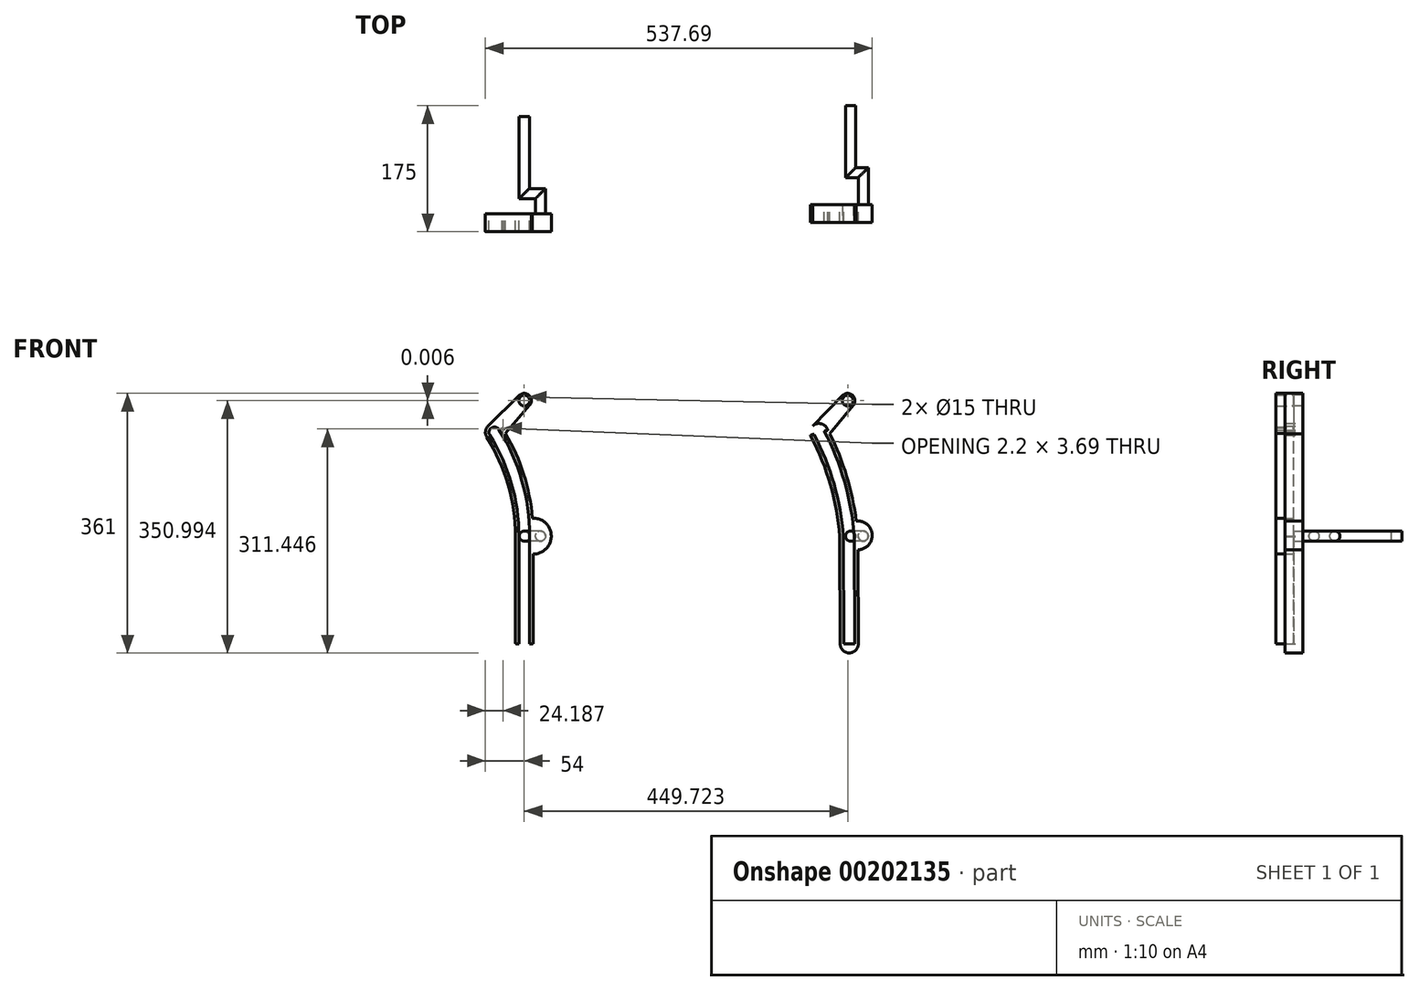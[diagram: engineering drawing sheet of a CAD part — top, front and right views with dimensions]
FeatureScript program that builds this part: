
annotation { "Feature Type Name" : "Feature", "Feature Type Description" : "" }
export const myFeature = defineFeature(function(context is Context, id is Id, definition is map)
    precondition{}
    {
        {
            var Q0;
            Q0=qCreatedBy(makeId("Front.planeOp"),FACE);
            var sketch = newSketch(context, id + "F0", { "sketchPlane" : qUnion([Q0])});
            skArc(sketch, "E0", {"start": v(451.22, 0) * mm, "mid": v(437.83, 74.2) * mm, "end": v(409.72, 144.14) * mm});
            skArc(sketch, "E1.0.startCap", {"start": v(458.7, 0.58) * mm, "mid": v(451.8, -7.48) * mm, "end": v(443.75, -0.58) * mm});
            skArc(sketch, "E1.0.endCap", {"start": v(403.08, 140.66) * mm, "mid": v(406.23, 150.78) * mm, "end": v(416.36, 147.63) * mm});
            skArc(sketch, "E1.0.left", {"start": v(443.75, -0.58) * mm, "mid": v(430.63, 72.12) * mm, "end": v(403.08, 140.66) * mm});
            skArc(sketch, "E1.0.right", {"start": v(458.7, 0.58) * mm, "mid": v(445.04, 76.27) * mm, "end": v(416.36, 147.63) * mm});
            skLineSegment(sketch, "E1.1.startCap", {"start": v(349.68, 0) * mm, "end": v(349.68, 0) * mm});
            skArc(sketch, "E2.0", {"start": v(463.69, 0.96) * mm, "mid": v(449.85, 77.65) * mm, "end": v(420.79, 149.96) * mm});
            skArc(sketch, "E3.0", {"start": v(438.72, -0.5) * mm, "mid": v(425.76, 70.95) * mm, "end": v(398.66, 138.33) * mm});
            skArc(sketch, "E4.0", {"start": v(398.66, 138.33) * mm, "mid": v(403.9, 155.2) * mm, "end": v(420.79, 149.96) * mm});
            skArc(sketch, "E5", {"start": v(463.8, -19.04) * mm, "mid": v(483.66, 2.04) * mm, "end": v(461.63, 20.85) * mm});
            skCircle(sketch, "E6", {"center": v(449.72, 188.5) * mm, "radius": 10 * mm});
            skLineSegment(sketch, "E7", {"start": v(442.58, 195.5) * mm, "end": v(400.8, 152.9) * mm});
            skLineSegment(sketch, "E8", {"start": v(457.42, 182.11) * mm, "end": v(419.35, 136.17) * mm});
            skLineSegment(sketch, "E9", {"start": v(451.22, 0) * mm, "end": v(451.8, -150) * mm});
            skPoint(sketch, "E9.endSnap0", {"position": v(451.8, -7.48) * mm});
            skArc(sketch, "E10.0.startCap", {"start": v(443.72, -0.03) * mm, "mid": v(451.2, 7.5) * mm, "end": v(458.72, 0.03) * mm});
            skArc(sketch, "E10.0.endCap", {"start": v(459.3, -149.97) * mm, "mid": v(451.83, -157.5) * mm, "end": v(444.3, -150.03) * mm});
            skLineSegment(sketch, "E10.0.left", {"start": v(458.72, 0.03) * mm, "end": v(459.3, -149.97) * mm});
            skLineSegment(sketch, "E10.0.right", {"start": v(443.72, -0.03) * mm, "end": v(444.3, -150.03) * mm});
            skLineSegment(sketch, "E11.0", {"start": v(463.72, 0.36) * mm, "end": v(464.3, -149.94) * mm});
            skLineSegment(sketch, "E12.0", {"start": v(438.72, -0.5) * mm, "end": v(439.3, -150.05) * mm});
            skArc(sketch, "E13.0", {"start": v(464.3, -149.94) * mm, "mid": v(451.85, -162.5) * mm, "end": v(439.3, -150.05) * mm});
            skLineSegment(sketch, "E14", {"start": v(438.72, -0.5) * mm, "end": v(463.69, 0.96) * mm});
            skCircle(sketch, "E15", {"center": v(451.22, 0) * mm, "radius": 188.5 * mm});
            skCircle(sketch, "E16", {"center": v(451.22, 0) * mm, "radius": 150 * mm});
            skSolve(sketch);
        }
        {
            var Q0;
            {var subQ0=sQuery(id+"F0.wireOp",EDGE,"E6");var subQ1=makeQuery(id+"F0.imprint","INTERSECT",VERTEX,{"derivedFrom":[subQ0,sQuery(id+"F0.wireOp",EDGE,"E7")]});Q0=makeQuery(id+"F0.imprint","IMPRINT",FACE,{"disambiguationData":[TD([[makeQuery(id+"F0.imprint","IMPRINT",EDGE,{"disambiguationData":[TD([[subQ1,-1.0]])],"derivedFrom":subQ0}),1.0]])]});}
            var Q1;
            {var subQ3=sQuery(id+"F0.wireOp",EDGE,"E5");Q1=makeQuery(id+"F0.imprint","IMPRINT",FACE,{"disambiguationData":[TD([[makeQuery(id+"F0.imprint","IMPRINT",EDGE,{"derivedFrom":subQ3}),1.0]])]});}
            var Q2;
            {var subQ5=sQuery(id+"F0.wireOp",EDGE,"E3.0");Q2=makeQuery(id+"F0.imprint","IMPRINT",FACE,{"disambiguationData":[TD([[makeQuery(id+"F0.imprint","IMPRINT",EDGE,{"derivedFrom":subQ5}),-1.0]])]});}
            var Q3;
            {var subQ0=sQuery(id+"F0.wireOp",EDGE,"E7");Q3=makeQuery(id+"F0.imprint","IMPRINT",FACE,{"disambiguationData":[TD([[makeQuery(id+"F0.imprint","IMPRINT",EDGE,{"derivedFrom":subQ0}),1.0]])]});}
            var Q4;
            {var subQ0=sQuery(id+"F0.wireOp",EDGE,"E10.0.right");Q4=makeQuery(id+"F0.imprint","IMPRINT",FACE,{"disambiguationData":[TD([[makeQuery(id+"F0.imprint","IMPRINT",EDGE,{"derivedFrom":subQ0}),-1.0]])]});}
            var Q5;
            {var subQ1=sQuery(id+"F0.wireOp",EDGE,"E2.0");var subQ5=makeQuery(id+"F0.imprint","INTERSECT",VERTEX,{"derivedFrom":[subQ1,sQuery(id+"F0.wireOp",EDGE,"E5")]});Q5=makeQuery(id+"F0.imprint","IMPRINT",FACE,{"disambiguationData":[TD([[makeQuery(id+"F0.imprint","IMPRINT",EDGE,{"disambiguationData":[TD([[subQ5,-1.0]])],"derivedFrom":subQ1}),1.0]])]});}
            var Q6;
            {var subQ0=sQuery(id+"F0.wireOp",EDGE,"E8");var subQ1=sQuery(id+"F0.wireOp",EDGE,"E1.0.right");var subQ2=makeQuery(id+"F0.imprint","INTERSECT",VERTEX,{"derivedFrom":[subQ1,subQ0]});Q6=makeQuery(id+"F0.imprint","IMPRINT",FACE,{"disambiguationData":[TD([[makeQuery(id+"F0.imprint","IMPRINT",EDGE,{"disambiguationData":[TD([[subQ2,-1.0]])],"derivedFrom":subQ1}),-1.0]])]});}
            var Q7;
            {var subQ6=sQuery(id+"F0.wireOp",EDGE,"E10.0.endCap");Q7=makeQuery(id+"F0.imprint","IMPRINT",FACE,{"disambiguationData":[TD([[makeQuery(id+"F0.imprint","IMPRINT",EDGE,{"derivedFrom":subQ6}),1.0]])]});}
            var Q8;
            {var subQ0=sQuery(id+"F0.wireOp",EDGE,"y67nMwY5-X2Z8-XgEG-YsyU-s40BRp6oOK45");var subQ1=sQuery(id+"F0.wireOp",EDGE,"zbyQ8gM6-2aZd-Salr-UTL1-q6hNuw3ZyB9F");var subQ2=makeQuery(id+"F0.imprint","INTERSECT",VERTEX,{"disambiguationData":[OD(0.0)],"derivedFrom":[subQ1,subQ0]});Q8=makeQuery(id+"F0.imprint","IMPRINT",FACE,{"disambiguationData":[TD([[makeQuery(id+"F0.imprint","IMPRINT",EDGE,{"disambiguationData":[TD([[subQ2,-1.0]])],"derivedFrom":subQ1}),-1.0]])]});}
            var Q9;
            {var subQ0=sQuery(id+"F0.wireOp",EDGE,"E6");var subQ1=makeQuery(id+"F0.imprint","INTERSECT",VERTEX,{"derivedFrom":[subQ0,sQuery(id+"F0.wireOp",EDGE,"E8")]});Q9=makeQuery(id+"F0.imprint","IMPRINT",FACE,{"disambiguationData":[TD([[makeQuery(id+"F0.imprint","IMPRINT",EDGE,{"disambiguationData":[TD([[subQ1,1.0]])],"derivedFrom":subQ0}),1.0]])]});}
            var Q10;
            {var subQ0=sQuery(id+"F0.wireOp",EDGE,"zbyQ8gM6-2aZd-Salr-UTL1-q6hNuw3ZyB9F");var subQ1=sQuery(id+"F0.wireOp",EDGE,"E2.0");var subQ2=makeQuery(id+"F0.imprint","INTERSECT",VERTEX,{"derivedFrom":[subQ1,subQ0]});Q10=makeQuery(id+"F0.imprint","IMPRINT",FACE,{"disambiguationData":[TD([[makeQuery(id+"F0.imprint","IMPRINT",EDGE,{"disambiguationData":[TD([[subQ2,1.0]])],"derivedFrom":subQ1}),-1.0]])]});}
            var Q11;
            {var subQ0=sQuery(id+"F0.wireOp",EDGE,"zbyQ8gM6-2aZd-Salr-UTL1-q6hNuw3ZyB9F");var subQ1=sQuery(id+"F0.wireOp",EDGE,"E1.0.left");var subQ2=makeQuery(id+"F0.imprint","INTERSECT",VERTEX,{"derivedFrom":[subQ1,subQ0]});Q11=makeQuery(id+"F0.imprint","IMPRINT",FACE,{"disambiguationData":[TD([[makeQuery(id+"F0.imprint","IMPRINT",EDGE,{"disambiguationData":[TD([[subQ2,1.0]])],"derivedFrom":subQ0}),-1.0]])]});}
            var Q12;
            {var subQ0=sQuery(id+"F0.wireOp",EDGE,"zbyQ8gM6-2aZd-Salr-UTL1-q6hNuw3ZyB9F");var subQ1=makeQuery(id+"F0.imprint","INTERSECT",VERTEX,{"derivedFrom":[subQ0,sQuery(id+"F0.wireOp",EDGE,"E7")]});Q12=makeQuery(id+"F0.imprint","IMPRINT",FACE,{"disambiguationData":[TD([[makeQuery(id+"F0.imprint","IMPRINT",EDGE,{"disambiguationData":[TD([[subQ1,1.0]])],"derivedFrom":subQ0}),1.0]])]});}
            var Q13;
            {var subQ4=sQuery(id+"F0.wireOp",EDGE,"E10.0.left");Q13=makeQuery(id+"F0.imprint","IMPRINT",FACE,{"disambiguationData":[TD([[makeQuery(id+"F0.imprint","IMPRINT",EDGE,{"derivedFrom":subQ4}),1.0]])]});}
            var Q14;
            {var subQ0=sQuery(id+"F0.wireOp",EDGE,"E8");var subQ1=sQuery(id+"F0.wireOp",EDGE,"E2.0");var subQ2=makeQuery(id+"F0.imprint","INTERSECT",VERTEX,{"derivedFrom":[subQ1,subQ0]});Q14=makeQuery(id+"F0.imprint","IMPRINT",FACE,{"disambiguationData":[TD([[makeQuery(id+"F0.imprint","IMPRINT",EDGE,{"disambiguationData":[TD([[subQ2,-1.0]])],"derivedFrom":subQ1}),-1.0]])]});}
            var Q15;
            {var subQ0=sQuery(id+"F0.wireOp",EDGE,"zbyQ8gM6-2aZd-Salr-UTL1-q6hNuw3ZyB9F");var subQ1=sQuery(id+"F0.wireOp",EDGE,"E1.0.right");var subQ2=makeQuery(id+"F0.imprint","INTERSECT",VERTEX,{"derivedFrom":[subQ1,subQ0]});Q15=makeQuery(id+"F0.imprint","IMPRINT",FACE,{"disambiguationData":[TD([[makeQuery(id+"F0.imprint","IMPRINT",EDGE,{"disambiguationData":[TD([[subQ2,-1.0]])],"derivedFrom":subQ1}),-1.0]])]});}
            var Q16;
            {var subQ6=sQuery(id+"F0.wireOp",EDGE,"E4.0");var subQ9=sQuery(id+"F0.wireOp",EDGE,"E2.0");var subQ10=makeQuery(id+"F0.imprint","INTERSECT",VERTEX,{"derivedFrom":[subQ9,subQ6]});Q16=makeQuery(id+"F0.imprint","IMPRINT",FACE,{"disambiguationData":[TD([[makeQuery(id+"F0.imprint","IMPRINT",EDGE,{"disambiguationData":[TD([[subQ10,1.0]])],"derivedFrom":subQ9}),-1.0]])]});}
            var Q17;
            {var subQ4=sQuery(id+"F0.wireOp",EDGE,"E1.0.right");var subQ5=sQuery(id+"F0.wireOp",EDGE,"E1.0.endCap");var subQ6=makeQuery(id+"F0.imprint","INTERSECT",VERTEX,{"derivedFrom":[subQ5,subQ4]});Q17=makeQuery(id+"F0.imprint","IMPRINT",FACE,{"disambiguationData":[TD([[makeQuery(id+"F0.imprint","IMPRINT",EDGE,{"disambiguationData":[TD([[subQ6,1.0]])],"derivedFrom":subQ5}),1.0]])]});}
            var Q18;
            {var subQ3=sQuery(id+"F0.wireOp",EDGE,"E1.0.left");var subQ7=sQuery(id+"F0.wireOp",EDGE,"E10.0.right");var subQ8=makeQuery(id+"F0.imprint","INTERSECT",VERTEX,{"derivedFrom":[subQ3,subQ7]});Q18=makeQuery(id+"F0.imprint","IMPRINT",FACE,{"disambiguationData":[TD([[makeQuery(id+"F0.imprint","IMPRINT",EDGE,{"disambiguationData":[TD([[subQ8,-1.0]])],"derivedFrom":subQ3}),1.0]])]});}
            extrude(context, id + "F1", {"entities" : qUnion([Q0, Q1, Q2, Q3, Q4, Q5, Q6, Q7, Q8, Q9, Q10, Q11, Q12, Q13, Q14, Q15, Q16, Q17, Q18]), "endBound" : BoundingType.SYMMETRIC, "depth" : 25 * mm});
        }
        {
            var Q0;
            Q0=qCreatedBy(makeId("Front.planeOp"),FACE);
            var sketch = newSketch(context, id + "F2", { "sketchPlane" : qUnion([Q0])});
            skCircle(sketch, "E17", {"center": v(471.19, 0) * mm, "radius": 7 * mm});
            skSolve(sketch);
        }
        {
            var Q0;
            Q0=qCreatedBy(makeId("Top.planeOp"),FACE);
            var sketch = newSketch(context, id + "F3", { "sketchPlane" : qUnion([Q0])});
            skLineSegment(sketch, "E18", {"start": v(464.19, 0) * mm, "end": v(464.19, 50) * mm});
            skLineSegment(sketch, "E19", {"start": v(464.19, 50) * mm, "end": v(446.69, 50) * mm});
            skLineSegment(sketch, "E20", {"start": v(446.69, 50) * mm, "end": v(446.69, 150) * mm});
            skSolve(sketch);
        }
        {
            var Q0;
            Q0 = qSketchRegion(id + "F2", true);
            var Q1;
            Q1 = qConstructionFilter(qBodyType(qCreatedBy(id + "F3" ,EDGE), BodyType.WIRE), ConstructionObject.NO);
            sweep(context, id + "F4", {"operationType" : NewBodyOperationType.ADD, "profiles" : qUnion([Q0]), "path" : qUnion([Q1])});
        }
        {
            var Q0;
            Q0=makeQuery(id+"F1.opExtrude","CAP_FACE",FACE,{"disambiguationData":[OSD([sQuery(id+"F0.wireOp",EDGE,"E1.0.endCap"),sQuery(id+"F0.wireOp",EDGE,"E1.0.left"),sQuery(id+"F0.wireOp",EDGE,"E1.0.right"),sQuery(id+"F0.wireOp",EDGE,"E2.0"),sQuery(id+"F0.wireOp",EDGE,"E3.0"),sQuery(id+"F0.wireOp",EDGE,"E5"),sQuery(id+"F0.wireOp",EDGE,"zbyQ8gM6-2aZd-Salr-UTL1-q6hNuw3ZyB9F"),sQuery(id+"F0.wireOp",EDGE,"E6"),sQuery(id+"F0.wireOp",EDGE,"E7"),sQuery(id+"F0.wireOp",EDGE,"E8"),sQuery(id+"F0.wireOp",EDGE,"E10.0.endCap"),sQuery(id+"F0.wireOp",EDGE,"E10.0.left"),sQuery(id+"F0.wireOp",EDGE,"E10.0.right"),sQuery(id+"F0.wireOp",EDGE,"E11.0"),sQuery(id+"F0.wireOp",EDGE,"E12.0"),sQuery(id+"F0.wireOp",EDGE,"E13.0")])],"isStart":false});
            var sketch = newSketch(context, id + "F5", { "sketchPlane" : qUnion([Q0])});
            skCircle(sketch, "E21", {"center": v(449.72, 188.5) * mm, "radius": 7.5 * mm});
            skSolve(sketch);
        }
        {
            var Q0;
            Q0 = qSketchRegion(id + "F5", true);
            extrude(context, id + "F6", {"entities" : qUnion([Q0]), "operationType" : NewBodyOperationType.REMOVE, "endBound" : BoundingType.THROUGH_ALL, "oppositeDirection" : true, "depth" : 25 * mm});
        }
        {
            var Q0;
            Q0=qCreatedBy(makeId("Front.planeOp"),FACE);
            var sketch = newSketch(context, id + "F7", { "sketchPlane" : qUnion([Q0])});
            skCircle(sketch, "E22", {"center": v(0, 0) * mm, "radius": 188.5 * mm});
            skCircle(sketch, "E23", {"center": v(0, 0) * mm, "radius": 150 * mm});
            skCircle(sketch, "E24", {"center": v(0, -150) * mm, "radius": 12.5 * mm});
            skCircle(sketch, "E25", {"center": v(0, 0) * mm, "radius": 12.5 * mm});
            skLineSegment(sketch, "E26", {"start": v(12.5, 0) * mm, "end": v(12.5, -150) * mm});
            skLineSegment(sketch, "E27", {"start": v(-12.5, -150) * mm, "end": v(-12.5, 0) * mm});
            skCircle(sketch, "E28", {"center": v(-41.5, 144.14) * mm, "radius": 12.5 * mm});
            skArc(sketch, "E29", {"start": v(12.5, 0) * mm, "mid": v(1.43, 78.46) * mm, "end": v(-30.91, 150.8) * mm});
            skArc(sketch, "E30", {"start": v(-12.5, 0) * mm, "mid": v(-22.6, 71.54) * mm, "end": v(-52.09, 137.5) * mm});
            skCircle(sketch, "E31", {"center": v(-41.5, 144.14) * mm, "radius": 7.5 * mm});
            skCircle(sketch, "E32", {"center": v(0, 0) * mm, "radius": 7.5 * mm});
            skCircle(sketch, "E33", {"center": v(0, -150) * mm, "radius": 7.5 * mm});
            skArc(sketch, "E34", {"start": v(7.5, 0) * mm, "mid": v(-3.37, 77.08) * mm, "end": v(-35.15, 148.13) * mm});
            skLineSegment(sketch, "E35", {"start": v(7.5, 0) * mm, "end": v(7.5, -150) * mm});
            skArc(sketch, "E36", {"start": v(-7.5, 0) * mm, "mid": v(-17.79, 72.93) * mm, "end": v(-47.85, 140.16) * mm});
            skLineSegment(sketch, "E37", {"start": v(-7.5, 0) * mm, "end": v(-7.5, -150) * mm});
            skCircle(sketch, "E38", {"center": v(0, 188.5) * mm, "radius": 10 * mm});
            skLineSegment(sketch, "E39", {"start": v(7.58, 181.97) * mm, "end": v(-32.03, 135.99) * mm});
            skLineSegment(sketch, "E40", {"start": v(-7.01, 195.63) * mm, "end": v(-50.27, 153.05) * mm});
            skCircle(sketch, "E41", {"center": v(0, 188.5) * mm, "radius": 7.5 * mm});
            skArc(sketch, "E42", {"start": v(12.5, -25) * mm, "mid": v(37.5, 0.55) * mm, "end": v(11.4, 24.98) * mm});
            skSolve(sketch);
        }
        {
            var Q0;
            {var subQ0=sQuery(id+"F7.wireOp",EDGE,"E40");var subQ1=sQuery(id+"F7.wireOp",EDGE,"E22");var subQ2=makeQuery(id+"F7.imprint","INTERSECT",VERTEX,{"derivedFrom":[subQ1,subQ0]});Q0=makeQuery(id+"F7.imprint","IMPRINT",FACE,{"disambiguationData":[TD([[makeQuery(id+"F7.imprint","IMPRINT",EDGE,{"disambiguationData":[TD([[subQ2,1.0]])],"derivedFrom":subQ1}),-1.0]])]});}
            var Q1;
            {var subQ0=sQuery(id+"F7.wireOp",EDGE,"E38");var subQ2=sQuery(id+"F7.wireOp",EDGE,"E22");var subQ3=makeQuery(id+"F7.imprint","INTERSECT",VERTEX,{"disambiguationData":[OD(0.0)],"derivedFrom":[subQ2,subQ0]});Q1=makeQuery(id+"F7.imprint","IMPRINT",FACE,{"disambiguationData":[TD([[makeQuery(id+"F7.imprint","IMPRINT",EDGE,{"disambiguationData":[TD([[subQ3,-1.0]])],"derivedFrom":subQ2}),-1.0]])]});}
            var Q2;
            {var subQ0=sQuery(id+"F7.wireOp",EDGE,"E38");var subQ2=sQuery(id+"F7.wireOp",EDGE,"E22");var subQ3=makeQuery(id+"F7.imprint","INTERSECT",VERTEX,{"disambiguationData":[OD(0.0)],"derivedFrom":[subQ2,subQ0]});Q2=makeQuery(id+"F7.imprint","IMPRINT",FACE,{"disambiguationData":[TD([[makeQuery(id+"F7.imprint","IMPRINT",EDGE,{"disambiguationData":[TD([[subQ3,-1.0]])],"derivedFrom":subQ2}),1.0]])]});}
            var Q3;
            {var subQ3=sQuery(id+"F7.wireOp",EDGE,"E40");var subQ11=sQuery(id+"F7.wireOp",EDGE,"E22");var subQ12=makeQuery(id+"F7.imprint","INTERSECT",VERTEX,{"derivedFrom":[subQ11,subQ3]});Q3=makeQuery(id+"F7.imprint","IMPRINT",FACE,{"disambiguationData":[TD([[makeQuery(id+"F7.imprint","IMPRINT",EDGE,{"disambiguationData":[TD([[subQ12,1.0]])],"derivedFrom":subQ11}),1.0]])]});}
            var Q4;
            {var subQ0=sQuery(id+"F7.wireOp",EDGE,"E29");var subQ1=sQuery(id+"F7.wireOp",EDGE,"E23");var subQ2=makeQuery(id+"F7.imprint","INTERSECT",VERTEX,{"derivedFrom":[subQ1,subQ0]});Q4=makeQuery(id+"F7.imprint","IMPRINT",FACE,{"disambiguationData":[TD([[makeQuery(id+"F7.imprint","IMPRINT",EDGE,{"disambiguationData":[TD([[subQ2,1.0]])],"derivedFrom":subQ1}),1.0]])]});}
            var Q5;
            {var subQ5=sQuery(id+"F7.wireOp",EDGE,"E29");var subQ6=sQuery(id+"F7.wireOp",EDGE,"E23");var subQ7=makeQuery(id+"F7.imprint","INTERSECT",VERTEX,{"derivedFrom":[subQ6,subQ5]});Q5=makeQuery(id+"F7.imprint","IMPRINT",FACE,{"disambiguationData":[TD([[makeQuery(id+"F7.imprint","IMPRINT",EDGE,{"disambiguationData":[TD([[subQ7,-1.0]])],"derivedFrom":subQ6}),1.0]])]});}
            var Q6;
            {var subQ0=sQuery(id+"F7.wireOp",EDGE,"E28");var subQ1=sQuery(id+"F7.wireOp",EDGE,"E23");var subQ2=makeQuery(id+"F7.imprint","INTERSECT",VERTEX,{"disambiguationData":[OD(0.0)],"derivedFrom":[subQ1,subQ0]});Q6=makeQuery(id+"F7.imprint","IMPRINT",FACE,{"disambiguationData":[TD([[makeQuery(id+"F7.imprint","IMPRINT",EDGE,{"disambiguationData":[TD([[subQ2,-1.0]])],"derivedFrom":subQ1}),1.0]])]});}
            var Q7;
            {var subQ0=sQuery(id+"F7.wireOp",EDGE,"E28");var subQ6=sQuery(id+"F7.wireOp",EDGE,"E23");var subQ8=makeQuery(id+"F7.imprint","INTERSECT",VERTEX,{"disambiguationData":[OD(0.0)],"derivedFrom":[subQ6,subQ0]});Q7=makeQuery(id+"F7.imprint","IMPRINT",FACE,{"disambiguationData":[TD([[makeQuery(id+"F7.imprint","IMPRINT",EDGE,{"disambiguationData":[TD([[subQ8,-1.0]])],"derivedFrom":subQ6}),-1.0]])]});}
            var Q8;
            {var subQ4=sQuery(id+"F7.wireOp",EDGE,"E23");var subQ6=sQuery(id+"F7.wireOp",EDGE,"E31");var subQ8=makeQuery(id+"F7.imprint","INTERSECT",VERTEX,{"disambiguationData":[OD(1.0)],"derivedFrom":[subQ4,subQ6]});Q8=makeQuery(id+"F7.imprint","IMPRINT",FACE,{"disambiguationData":[TD([[makeQuery(id+"F7.imprint","IMPRINT",EDGE,{"disambiguationData":[TD([[subQ8,-1.0]])],"derivedFrom":subQ4}),1.0]])]});}
            var Q9;
            {var subQ0=sQuery(id+"F7.wireOp",EDGE,"E30");Q9=makeQuery(id+"F7.imprint","IMPRINT",FACE,{"disambiguationData":[TD([[makeQuery(id+"F7.imprint","IMPRINT",EDGE,{"derivedFrom":subQ0}),-1.0]])]});}
            var Q10;
            {var subQ1=sQuery(id+"F7.wireOp",EDGE,"E25");var subQ3=sQuery(id+"F7.wireOp",EDGE,"E34");var subQ4=makeQuery(id+"F7.imprint","INTERSECT",VERTEX,{"derivedFrom":[subQ1,subQ3]});Q10=makeQuery(id+"F7.imprint","IMPRINT",FACE,{"disambiguationData":[TD([[makeQuery(id+"F7.imprint","IMPRINT",EDGE,{"disambiguationData":[TD([[subQ4,-1.0]])],"derivedFrom":subQ3}),-1.0]])]});}
            var Q11;
            {var subQ0=sQuery(id+"F7.wireOp",EDGE,"E25");var subQ2=sQuery(id+"F7.wireOp",EDGE,"E34");var subQ3=makeQuery(id+"F7.imprint","INTERSECT",VERTEX,{"derivedFrom":[subQ0,subQ2]});Q11=makeQuery(id+"F7.imprint","IMPRINT",FACE,{"disambiguationData":[TD([[makeQuery(id+"F7.imprint","IMPRINT",EDGE,{"disambiguationData":[TD([[subQ3,1.0]])],"derivedFrom":subQ0}),1.0]])]});}
            var Q12;
            {var subQ3=sQuery(id+"F7.wireOp",EDGE,"E23");var subQ5=sQuery(id+"F7.wireOp",EDGE,"E24");var subQ6=makeQuery(id+"F7.imprint","INTERSECT",VERTEX,{"disambiguationData":[OD(1.0)],"derivedFrom":[subQ3,subQ5]});Q12=makeQuery(id+"F7.imprint","IMPRINT",FACE,{"disambiguationData":[TD([[makeQuery(id+"F7.imprint","IMPRINT",EDGE,{"disambiguationData":[TD([[subQ6,-1.0]])],"derivedFrom":subQ3}),1.0]])]});}
            var Q13;
            {var subQ0=sQuery(id+"F7.wireOp",EDGE,"E35");var subQ1=sQuery(id+"F7.wireOp",EDGE,"E23");var subQ2=makeQuery(id+"F7.imprint","INTERSECT",VERTEX,{"derivedFrom":[subQ1,subQ0]});Q13=makeQuery(id+"F7.imprint","IMPRINT",FACE,{"disambiguationData":[TD([[makeQuery(id+"F7.imprint","IMPRINT",EDGE,{"disambiguationData":[TD([[subQ2,-1.0]])],"derivedFrom":subQ1}),1.0]])]});}
            var Q14;
            {var subQ0=sQuery(id+"F7.wireOp",EDGE,"E24");var subQ1=sQuery(id+"F7.wireOp",EDGE,"E23");var subQ2=makeQuery(id+"F7.imprint","INTERSECT",VERTEX,{"disambiguationData":[OD(0.0)],"derivedFrom":[subQ1,subQ0]});Q14=makeQuery(id+"F7.imprint","IMPRINT",FACE,{"disambiguationData":[TD([[makeQuery(id+"F7.imprint","IMPRINT",EDGE,{"disambiguationData":[TD([[subQ2,-1.0]])],"derivedFrom":subQ1}),1.0]])]});}
            var Q15;
            {var subQ0=sQuery(id+"F7.wireOp",EDGE,"E27");var subQ3=sQuery(id+"F7.wireOp",EDGE,"E23");var subQ4=makeQuery(id+"F7.imprint","INTERSECT",VERTEX,{"derivedFrom":[subQ3,subQ0]});Q15=makeQuery(id+"F7.imprint","IMPRINT",FACE,{"disambiguationData":[TD([[makeQuery(id+"F7.imprint","IMPRINT",EDGE,{"disambiguationData":[TD([[subQ4,-1.0]])],"derivedFrom":subQ3}),1.0]])]});}
            var Q16;
            {var subQ0=sQuery(id+"F7.wireOp",EDGE,"E25");var subQ2=sQuery(id+"F7.wireOp",EDGE,"E36");var subQ3=makeQuery(id+"F7.imprint","INTERSECT",VERTEX,{"derivedFrom":[subQ0,subQ2]});Q16=makeQuery(id+"F7.imprint","IMPRINT",FACE,{"disambiguationData":[TD([[makeQuery(id+"F7.imprint","IMPRINT",EDGE,{"disambiguationData":[TD([[subQ3,-1.0]])],"derivedFrom":subQ0}),1.0]])]});}
            var Q17;
            {var subQ0=sQuery(id+"F7.wireOp",EDGE,"E24");var subQ2=sQuery(id+"F7.wireOp",EDGE,"E23");var subQ3=makeQuery(id+"F7.imprint","INTERSECT",VERTEX,{"disambiguationData":[OD(0.0)],"derivedFrom":[subQ2,subQ0]});Q17=makeQuery(id+"F7.imprint","IMPRINT",FACE,{"disambiguationData":[TD([[makeQuery(id+"F7.imprint","IMPRINT",EDGE,{"disambiguationData":[TD([[subQ3,-1.0]])],"derivedFrom":subQ2}),-1.0]])]});}
            var Q18;
            {var subQ3=sQuery(id+"F7.wireOp",EDGE,"E42");Q18=makeQuery(id+"F7.imprint","IMPRINT",FACE,{"disambiguationData":[TD([[makeQuery(id+"F7.imprint","IMPRINT",EDGE,{"derivedFrom":subQ3}),1.0]])]});}
            extrude(context, id + "F8", {"entities" : qUnion([Q0, Q1, Q2, Q3, Q4, Q5, Q6, Q7, Q8, Q9, Q10, Q11, Q12, Q13, Q14, Q15, Q16, Q17, Q18]), "depth" : 25 * mm});
        }
        {
            var Q0;
            Q0=makeQuery(id+"F8.opExtrude","CAP_FACE",FACE,{"disambiguationData":[OSD([sQuery(id+"F7.wireOp",EDGE,"E23"),sQuery(id+"F7.wireOp",EDGE,"E24"),sQuery(id+"F7.wireOp",EDGE,"E26"),sQuery(id+"F7.wireOp",EDGE,"E27"),sQuery(id+"F7.wireOp",EDGE,"E28"),sQuery(id+"F7.wireOp",EDGE,"E29"),sQuery(id+"F7.wireOp",EDGE,"E30"),sQuery(id+"F7.wireOp",EDGE,"E31"),sQuery(id+"F7.wireOp",EDGE,"E33"),sQuery(id+"F7.wireOp",EDGE,"E34"),sQuery(id+"F7.wireOp",EDGE,"E35"),sQuery(id+"F7.wireOp",EDGE,"E36"),sQuery(id+"F7.wireOp",EDGE,"E37"),sQuery(id+"F7.wireOp",EDGE,"E38"),sQuery(id+"F7.wireOp",EDGE,"E39"),sQuery(id+"F7.wireOp",EDGE,"E40"),sQuery(id+"F7.wireOp",EDGE,"E41"),sQuery(id+"F7.wireOp",EDGE,"E42")])],"isStart":true});
            var sketch = newSketch(context, id + "F9", { "sketchPlane" : qUnion([Q0])});
            skCircle(sketch, "E43", {"center": v(-22.5, 0) * mm, "radius": 7 * mm});
            skSolve(sketch);
        }
        {
            var Q0;
            Q0=qCreatedBy(makeId("Top.planeOp"),FACE);
            var sketch = newSketch(context, id + "F10", { "sketchPlane" : qUnion([Q0])});
            skLineSegment(sketch, "E44", {"start": v(29.5, 0) * mm, "end": v(29.5, 35) * mm});
            skLineSegment(sketch, "E45", {"start": v(29.5, 35) * mm, "end": v(7, 35) * mm});
            skLineSegment(sketch, "E46", {"start": v(7, 35) * mm, "end": v(7, 135) * mm});
            skSolve(sketch);
        }
        {
            var Q0;
            Q0=makeQuery(id+"F9.imprint","IMPRINT",FACE,{"disambiguationData":[TD([[makeQuery(id+"F9.imprint","IMPRINT",EDGE,{"derivedFrom":sQuery(id+"F9.wireOp",EDGE,"E43")}),1.0]])]});
            var Q1;
            Q1=sQuery(id+"F10.wireOp",EDGE,"E44");
            var Q2;
            Q2=sQuery(id+"F10.wireOp",EDGE,"E45");
            var Q3;
            Q3=sQuery(id+"F10.wireOp",EDGE,"E46");
            sweep(context, id + "F11", {"operationType" : NewBodyOperationType.ADD, "profiles" : qUnion([Q0]), "path" : qUnion([Q1, Q2, Q3])});
        }
    });
